# Revit family: Furniture-Table-Midmark-626-Power_Examination1
name_source: partatom
category: Furniture
revit_build: Autodesk Revit 2016 (Build: 20170117_1200(x64)
units: mm (PartAtom-declared; Revit-internal decimal feet)

## family parameters
Always vertical = Yes
Cut with Voids When Loaded = No
OmniClass Number = 23.40.70.11.14.11.14
OmniClass Title = Examination and Treatment Equipment
Room Calculation Point = No
Shared = No
Work Plane-Based = No

## types (4) — shared parameters
Amps = 12 A
Apparent Load = 1380 VA
Assembly Code = E1020810
Connector Description = Power Connector
Description = Midmark 626 Barrier-Free Power Examination Table
Manufacturer = Midmark
Model = Midmark 626
Number of Poles = 1
Patient Weight Capacity = 650.00 lb
Power Factor = 1
Product Documentation Link = http://www.midmark.com
Product Page URL = http://www.midmark.com
URL = http://www.midmark.com
Voltage = 115 V
Weight = 435.00 lb

## type names (no varying parameters)
- 626-001
- 626-002
- 626-003
- 626-004

## geometry (parser evidence)
native form markers: Blend x6, Sweep x23
no freeform markers — native parametric forms only
